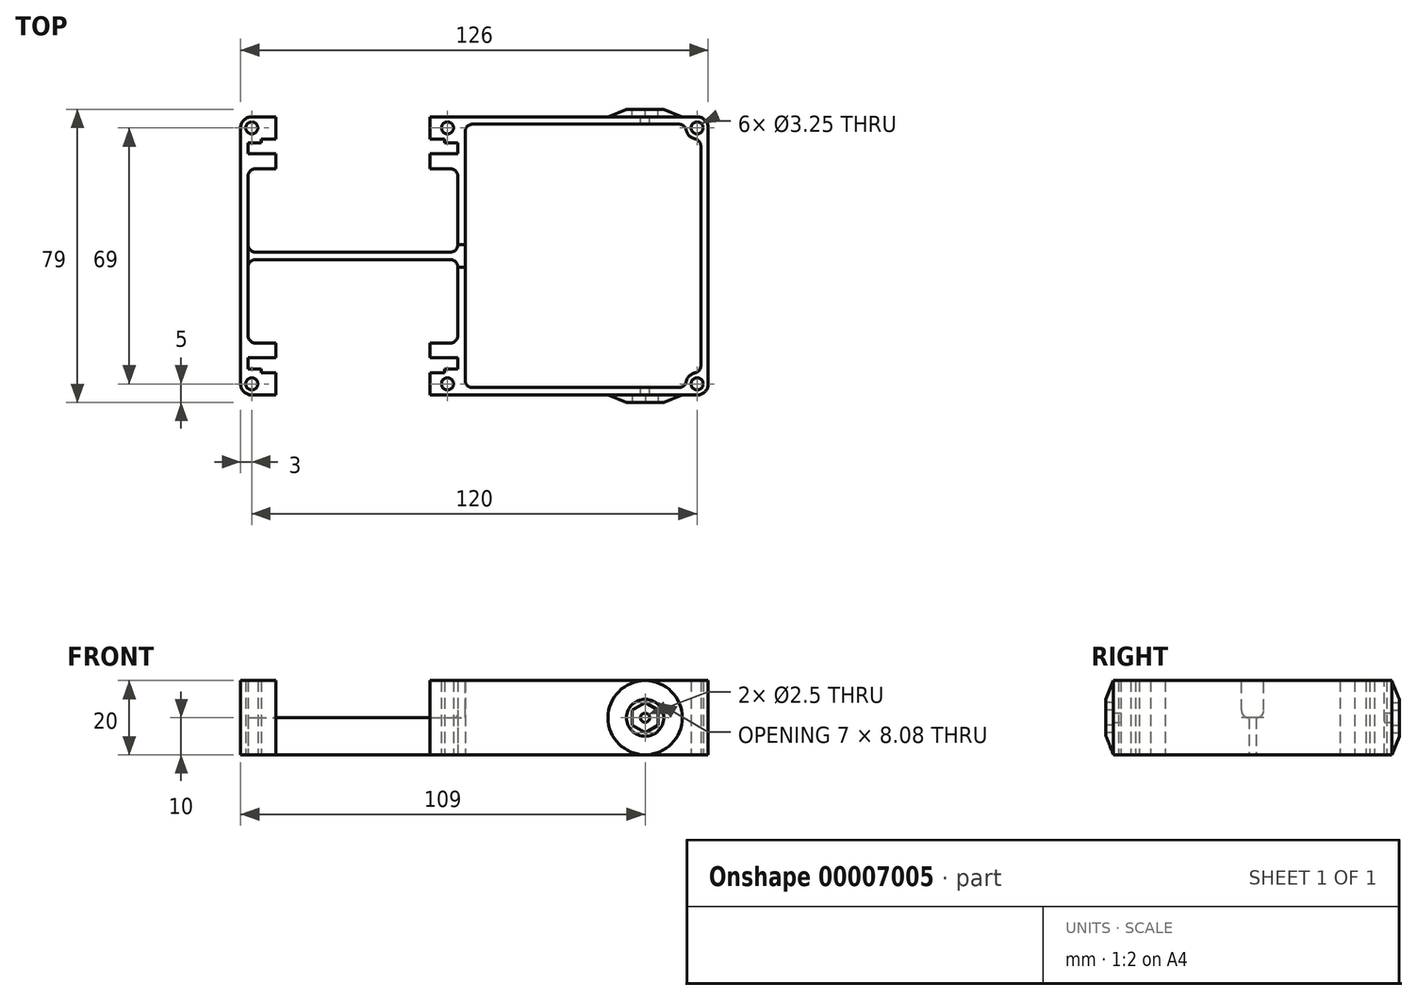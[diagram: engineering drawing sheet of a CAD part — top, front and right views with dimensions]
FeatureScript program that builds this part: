
annotation { "Feature Type Name" : "Feature", "Feature Type Description" : "" }
export const myFeature = defineFeature(function(context is Context, id is Id, definition is map)
    precondition{}
    {
        {
            var Q0;
            Q0=qCreatedBy(makeId("Top.planeOp"),FACE);
            var sketch = newSketch(context, id + "F0", { "sketchPlane" : qUnion([Q0])});
            skLineSegment(sketch, "E0.0", {"start": v(41, 72) * mm, "end": v(41, 66) * mm});
            skLineSegment(sketch, "E1.0", {"start": v(-7.5, 62) * mm, "end": v(-0.5, 62) * mm});
            skLineSegment(sketch, "E2.0", {"start": v(-8, 65) * mm, "end": v(-8, 62.5) * mm});
            skLineSegment(sketch, "E3.0", {"start": v(41, 62) * mm, "end": v(48, 62) * mm});
            skLineSegment(sketch, "E4.0", {"start": v(48.5, 62.5) * mm, "end": v(48.5, 65) * mm});
            skLineSegment(sketch, "E5.trimOffspring", {"start": v(-0.5, 66) * mm, "end": v(-0.5, 72) * mm});
            skLineSegment(sketch, "E6", {"start": v(-8, 62.5) * mm, "end": v(-8, 62) * mm});
            skLineSegment(sketch, "E7", {"start": v(-8, 62) * mm, "end": v(-7.5, 62) * mm});
            skLineSegment(sketch, "E8", {"start": v(48, 62) * mm, "end": v(48.5, 62) * mm});
            skLineSegment(sketch, "E9", {"start": v(48.5, 62) * mm, "end": v(48.5, 62.5) * mm});
            skLineSegment(sketch, "E10", {"start": v(45, 65) * mm, "end": v(48.5, 65) * mm});
            skLineSegment(sketch, "E11", {"start": v(-8, 65) * mm, "end": v(-4.5, 65) * mm});
            skLineSegment(sketch, "E12", {"start": v(-0.5, 66) * mm, "end": v(-4.5, 66) * mm});
            skLineSegment(sketch, "E13", {"start": v(-4.5, 66) * mm, "end": v(-4.5, 65) * mm});
            skLineSegment(sketch, "E14", {"start": v(41, 66) * mm, "end": v(45, 66) * mm});
            skLineSegment(sketch, "E15", {"start": v(45, 66) * mm, "end": v(45, 65) * mm});
            skLineSegment(sketch, "E16", {"start": v(-0.5, 62) * mm, "end": v(-0.5, 58) * mm});
            skLineSegment(sketch, "E17", {"start": v(41, 62) * mm, "end": v(41, 58) * mm});
            skLineSegment(sketch, "E18", {"start": v(-0.5, 58) * mm, "end": v(-8, 58) * mm});
            skLineSegment(sketch, "E19", {"start": v(41, 58) * mm, "end": v(48.5, 58) * mm});
            skLineSegment(sketch, "E20", {"start": v(-0.5, 72) * mm, "end": v(-10, 72) * mm});
            skLineSegment(sketch, "E21", {"start": v(41, 72) * mm, "end": v(116, 72) * mm});
            skLineSegment(sketch, "E22.1", {"start": v(50.5, 70) * mm, "end": v(110.17, 70) * mm});
            skPoint(sketch, "E23.endSnap0", {"position": v(41, 69) * mm});
            skCircle(sketch, "E24", {"center": v(45.75, 69) * mm, "radius": 1.63 * mm});
            skCircle(sketch, "E25", {"center": v(-7, 69) * mm, "radius": 1.63 * mm});
            skCircle(sketch, "E26", {"center": v(113, 69) * mm, "radius": 1.63 * mm});
            skArc(sketch, "E27.trimOffspring", {"start": v(110.17, 70) * mm, "mid": v(110.88, 66.88) * mm, "end": v(114, 66.17) * mm});
            skLineSegment(sketch, "E28", {"start": v(-8, 58) * mm, "end": v(-8, 35.5) * mm});
            skLineSegment(sketch, "E29", {"start": v(-8, 35.5) * mm, "end": v(48.5, 35.5) * mm});
            skLineSegment(sketch, "E30", {"start": v(48.5, 35.5) * mm, "end": v(48.5, 58) * mm});
            skLineSegment(sketch, "E31.MirrorCS", {"start": v(-8, 7) * mm, "end": v(-7.5, 7) * mm});
            skLineSegment(sketch, "E32.MirrorCS", {"start": v(48.5, 6.5) * mm, "end": v(48.5, 4) * mm});
            skLineSegment(sketch, "E33.MirrorCS", {"start": v(-8, 4) * mm, "end": v(-8, 6.5) * mm});
            skLineSegment(sketch, "E34.MirrorCS", {"start": v(-4.5, 3) * mm, "end": v(-4.5, 4) * mm});
            skLineSegment(sketch, "E35.MirrorCS", {"start": v(-0.5, 7) * mm, "end": v(-0.5, 11) * mm});
            skLineSegment(sketch, "E36.MirrorCS", {"start": v(-0.5, 3) * mm, "end": v(-4.5, 3) * mm});
            skCircle(sketch, "E37.MirrorC", {"center": v(113, 0) * mm, "radius": 1.63 * mm});
            skCircle(sketch, "E38.MirrorC", {"center": v(-7, 0) * mm, "radius": 1.63 * mm});
            skLineSegment(sketch, "E39.MirrorCS", {"start": v(45, 4) * mm, "end": v(48.5, 4) * mm});
            skLineSegment(sketch, "E40.MirrorCS", {"start": v(45, 3) * mm, "end": v(45, 4) * mm});
            skLineSegment(sketch, "E41.MirrorCS", {"start": v(-8, 4) * mm, "end": v(-4.5, 4) * mm});
            skLineSegment(sketch, "E42.MirrorCS", {"start": v(41, 7) * mm, "end": v(41, 11) * mm});
            skLineSegment(sketch, "E43.MirrorCS", {"start": v(41, 3) * mm, "end": v(45, 3) * mm});
            skLineSegment(sketch, "E44.MirrorCS", {"start": v(-0.5, -3) * mm, "end": v(-10, -3) * mm});
            skArc(sketch, "E45.MirrorCS", {"start": v(110.17, -1) * mm, "mid": v(110.88, 2.12) * mm, "end": v(114, 2.83) * mm});
            skCircle(sketch, "E46.MirrorC", {"center": v(45.75, 0) * mm, "radius": 1.63 * mm});
            skLineSegment(sketch, "E47.MirrorCS", {"start": v(-7.5, 7) * mm, "end": v(-0.5, 7) * mm});
            skLineSegment(sketch, "E48.MirrorCS", {"start": v(41, -3) * mm, "end": v(41, 3) * mm});
            skLineSegment(sketch, "E49.MirrorCS", {"start": v(-8, 33.5) * mm, "end": v(48.5, 33.5) * mm});
            skLineSegment(sketch, "E50.MirrorCS", {"start": v(41, 7) * mm, "end": v(48, 7) * mm});
            skLineSegment(sketch, "E51.MirrorCS", {"start": v(48.5, 33.5) * mm, "end": v(48.5, 11) * mm});
            skLineSegment(sketch, "E52.MirrorCS", {"start": v(-0.5, 3) * mm, "end": v(-0.5, -3) * mm});
            skPoint(sketch, "E53.MirrorP", {"position": v(41, 0) * mm});
            skLineSegment(sketch, "E54.MirrorCS", {"start": v(-0.5, 11) * mm, "end": v(-8, 11) * mm});
            skLineSegment(sketch, "E55.MirrorCS", {"start": v(41, 11) * mm, "end": v(48.5, 11) * mm});
            skLineSegment(sketch, "E56.MirrorCS", {"start": v(41, -3) * mm, "end": v(116, -3) * mm});
            skLineSegment(sketch, "E57.MirrorCS", {"start": v(-8, 11) * mm, "end": v(-8, 33.5) * mm});
            skLineSegment(sketch, "E58.MirrorCS", {"start": v(50.5, -1) * mm, "end": v(110.17, -1) * mm});
            skLineSegment(sketch, "E59", {"start": v(116, 72) * mm, "end": v(116, -3) * mm});
            skLineSegment(sketch, "E60", {"start": v(114, 2.83) * mm, "end": v(114, 66.17) * mm});
            skLineSegment(sketch, "E61", {"start": v(-10, 72) * mm, "end": v(-10, -3) * mm});
            skLineSegment(sketch, "E62", {"start": v(-8, 7) * mm, "end": v(-8, 6.5) * mm});
            skLineSegment(sketch, "E63", {"start": v(48, 7) * mm, "end": v(48.5, 7) * mm});
            skLineSegment(sketch, "E64", {"start": v(48.5, 7) * mm, "end": v(48.5, 6.5) * mm});
            skLineSegment(sketch, "E65", {"start": v(50.5, 70) * mm, "end": v(50.5, -1) * mm});
            skSolve(sketch);
        }
        {
            var Q0;
            Q0=makeQuery(id+"F0.imprint","IMPRINT",FACE,{"disambiguationData":[TD([[makeQuery(id+"F0.imprint","IMPRINT",EDGE,{"derivedFrom":sQuery(id+"F0.wireOp",EDGE,"E0.0")}),1.0]])]});
            extrude(context, id + "F1", {"entities" : qUnion([Q0]), "depth" : 20 * mm});
        }
        {
            var Q0;
            Q0=makeQuery(id+"F1.opExtrude","SWEPT_FACE",FACE,{"disambiguationData":[OSD([sQuery(id+"F0.wireOp",EDGE,"E21")])]});
            var sketch = newSketch(context, id + "F2", { "sketchPlane" : qUnion([Q0])});
            skCircle(sketch, "E66", {"center": v(-99, 10) * mm, "radius": 10 * mm});
            skPoint(sketch, "E66.centerSnap0", {"position": v(-113, 10) * mm});
            skSolve(sketch);
        }
        {
            var Q0;
            Q0=qSketchRegion(id+"F2",true);
            extrude(context, id + "F3", {"entities" : qUnion([Q0]), "operationType" : NewBodyOperationType.ADD, "depth" : 2 * mm});
        }
        {
            var Q0;
            Q0=makeQuery(id+"F3.opExtrude","CAP_EDGE",EDGE,{"disambiguationData":[OSD([sQuery(id+"F2.wireOp",EDGE,"E66")])],"isStart":false});
            chamfer(context, id + "F4", {"entities" : qUnion([Q0]), "chamferType" : ChamferType.TWO_OFFSETS, "width1" : 5 * mm, "oppositeDirection" : false, "width2" : 2 * mm, "tangentPropagation" : true});
        }
        {
            var Q0;
            Q0=makeQuery(id+"F3.opExtrude","CAP_FACE",FACE,{"disambiguationData":[OSD([sQuery(id+"F2.wireOp",EDGE,"E66")])],"isStart":false});
            var sketch = newSketch(context, id + "F5", { "sketchPlane" : qUnion([Q0])});
            skCircle(sketch, "E67", {"center": v(-99, 10) * mm, "radius": 1.25 * mm});
            skSolve(sketch);
        }
        {
            var Q0;
            Q0=makeQuery(id+"F1.opExtrude","SWEPT_FACE",FACE,{"disambiguationData":[OSD([sQuery(id+"F0.wireOp",EDGE,"E56.MirrorCS")])]});
            var sketch = newSketch(context, id + "F6", { "sketchPlane" : qUnion([Q0])});
            skCircle(sketch, "E68", {"center": v(99, 10) * mm, "radius": 10 * mm});
            skSolve(sketch);
        }
        {
            var Q0;
            Q0=qSketchRegion(id+"F6",true);
            extrude(context, id + "F7", {"entities" : qUnion([Q0]), "operationType" : NewBodyOperationType.ADD, "depth" : 2 * mm});
        }
        {
            var Q0;
            Q0=makeQuery(id+"F5.imprint","IMPRINT",FACE,{"disambiguationData":[TD([[makeQuery(id+"F5.imprint","IMPRINT",EDGE,{"derivedFrom":sQuery(id+"F5.wireOp",EDGE,"E67")}),1.0]])]});
            extrude(context, id + "F8", {"entities" : qUnion([Q0]), "operationType" : NewBodyOperationType.REMOVE, "oppositeDirection" : true, "depth" : 100 * mm});
        }
        {
            var Q0;
            Q0=makeQuery(id+"F7.opExtrude","CAP_EDGE",EDGE,{"disambiguationData":[OSD([sQuery(id+"F6.wireOp",EDGE,"E68")])],"isStart":false});
            chamfer(context, id + "F9", {"entities" : qUnion([Q0]), "chamferType" : ChamferType.TWO_OFFSETS, "width1" : 5 * mm, "oppositeDirection" : false, "width2" : 2 * mm, "tangentPropagation" : true});
        }
        {
            var Q0;
            Q0=makeQuery(id+"F1.opExtrude","SWEPT_EDGE",EDGE,{"disambiguationData":[OSD([sQuery(id+"F0.wireOp",EDGE,"E44.MirrorCS"),sQuery(id+"F0.wireOp",EDGE,"E61")])]});
            var Q1;
            Q1=makeQuery(id+"F1.opExtrude","SWEPT_EDGE",EDGE,{"disambiguationData":[OSD([sQuery(id+"F0.wireOp",EDGE,"E56.MirrorCS"),sQuery(id+"F0.wireOp",EDGE,"E59")])]});
            var Q2;
            Q2=makeQuery(id+"F1.opExtrude","SWEPT_EDGE",EDGE,{"disambiguationData":[OSD([sQuery(id+"F0.wireOp",EDGE,"E21"),sQuery(id+"F0.wireOp",EDGE,"E59")])]});
            var Q3;
            Q3=makeQuery(id+"F1.opExtrude","SWEPT_EDGE",EDGE,{"disambiguationData":[OSD([sQuery(id+"F0.wireOp",EDGE,"E20"),sQuery(id+"F0.wireOp",EDGE,"E61")])]});
            fillet(context, id + "F10", {"entities" : qUnion([Q0, Q1, Q2, Q3]), "radius" : 3 * mm, "tangentPropagation" : true, "allowEdgeOverflow" : false});
        }
        {
            var Q0;
            Q0=makeQuery(id+"F1.opExtrude","SWEPT_EDGE",EDGE,{"disambiguationData":[OSD([sQuery(id+"F0.wireOp",EDGE,"E45.MirrorCS"),sQuery(id+"F0.wireOp",EDGE,"E58.MirrorCS")])]});
            var Q1;
            Q1=makeQuery(id+"F1.opExtrude","SWEPT_EDGE",EDGE,{"disambiguationData":[OSD([sQuery(id+"F0.wireOp",EDGE,"E45.MirrorCS"),sQuery(id+"F0.wireOp",EDGE,"E60")])]});
            var Q2;
            Q2=makeQuery(id+"F1.opExtrude","SWEPT_EDGE",EDGE,{"disambiguationData":[OSD([sQuery(id+"F0.wireOp",EDGE,"E58.MirrorCS"),sQuery(id+"F0.wireOp",EDGE,"E65")])]});
            var Q3;
            Q3=makeQuery(id+"F1.opExtrude","SWEPT_EDGE",EDGE,{"disambiguationData":[OSD([sQuery(id+"F0.wireOp",EDGE,"E22.1"),sQuery(id+"F0.wireOp",EDGE,"E65")])]});
            var Q4;
            Q4=makeQuery(id+"F1.opExtrude","SWEPT_EDGE",EDGE,{"disambiguationData":[OSD([sQuery(id+"F0.wireOp",EDGE,"E22.1"),sQuery(id+"F0.wireOp",EDGE,"E27.trimOffspring")])]});
            var Q5;
            Q5=makeQuery(id+"F1.opExtrude","SWEPT_EDGE",EDGE,{"disambiguationData":[OSD([sQuery(id+"F0.wireOp",EDGE,"E27.trimOffspring"),sQuery(id+"F0.wireOp",EDGE,"E60")])]});
            var Q6;
            Q6=makeQuery(id+"F1.opExtrude","SWEPT_EDGE",EDGE,{"disambiguationData":[OSD([sQuery(id+"F0.wireOp",EDGE,"E49.MirrorCS"),sQuery(id+"F0.wireOp",EDGE,"E57.MirrorCS")])]});
            var Q7;
            Q7=makeQuery(id+"F1.opExtrude","SWEPT_EDGE",EDGE,{"disambiguationData":[OSD([sQuery(id+"F0.wireOp",EDGE,"E28"),sQuery(id+"F0.wireOp",EDGE,"E29")])]});
            var Q8;
            Q8=makeQuery(id+"F1.opExtrude","SWEPT_EDGE",EDGE,{"disambiguationData":[OSD([sQuery(id+"F0.wireOp",EDGE,"E29"),sQuery(id+"F0.wireOp",EDGE,"E30")])]});
            var Q9;
            Q9=makeQuery(id+"F1.opExtrude","SWEPT_EDGE",EDGE,{"disambiguationData":[OSD([sQuery(id+"F0.wireOp",EDGE,"E49.MirrorCS"),sQuery(id+"F0.wireOp",EDGE,"E51.MirrorCS")])]});
            var Q10;
            Q10=makeQuery(id+"F1.opExtrude","SWEPT_EDGE",EDGE,{"disambiguationData":[OSD([sQuery(id+"F0.wireOp",EDGE,"E19"),sQuery(id+"F0.wireOp",EDGE,"E30")])]});
            var Q11;
            Q11=makeQuery(id+"F1.opExtrude","SWEPT_EDGE",EDGE,{"disambiguationData":[OSD([sQuery(id+"F0.wireOp",EDGE,"E18"),sQuery(id+"F0.wireOp",EDGE,"E28")])]});
            var Q12;
            Q12=makeQuery(id+"F1.opExtrude","SWEPT_EDGE",EDGE,{"disambiguationData":[OSD([sQuery(id+"F0.wireOp",EDGE,"E54.MirrorCS"),sQuery(id+"F0.wireOp",EDGE,"E57.MirrorCS")])]});
            var Q13;
            Q13=makeQuery(id+"F1.opExtrude","SWEPT_EDGE",EDGE,{"disambiguationData":[OSD([sQuery(id+"F0.wireOp",EDGE,"E51.MirrorCS"),sQuery(id+"F0.wireOp",EDGE,"E55.MirrorCS")])]});
            fillet(context, id + "F11", {"entities" : qUnion([Q0, Q1, Q2, Q3, Q4, Q5, Q6, Q7, Q8, Q9, Q10, Q11, Q12, Q13]), "radius" : 2 * mm, "tangentPropagation" : true, "allowEdgeOverflow" : false});
        }
        {
            var Q0;
            Q0=makeQuery(id+"F3.opExtrude","CAP_FACE",FACE,{"disambiguationData":[OSD([sQuery(id+"F2.wireOp",EDGE,"E66")])],"isStart":false});
            var sketch = newSketch(context, id + "F12", { "sketchPlane" : qUnion([Q0])});
            skCircle(sketch, "E69.cCircle", {"center": v(-99, 10) * mm, "radius": 3.5 * mm, "construction": true});
            skLineSegment(sketch, "E69.0", {"start": v(-95.5, 12.02) * mm, "end": v(-95.5, 7.98) * mm});
            skLineSegment(sketch, "E69.1", {"start": v(-95.5, 7.98) * mm, "end": v(-99, 5.96) * mm});
            skLineSegment(sketch, "E69.2", {"start": v(-99, 5.96) * mm, "end": v(-102.5, 7.98) * mm});
            skLineSegment(sketch, "E69.3", {"start": v(-102.5, 7.98) * mm, "end": v(-102.5, 12.02) * mm});
            skLineSegment(sketch, "E69.4", {"start": v(-102.5, 12.02) * mm, "end": v(-99, 14.04) * mm});
            skLineSegment(sketch, "E69.5", {"start": v(-99, 14.04) * mm, "end": v(-95.5, 12.02) * mm});
            skPoint(sketch, "E69.0.midPoint", {"position": v(-95.5, 10) * mm});
            skSolve(sketch);
        }
        {
            var Q0;
            Q0=makeQuery(id+"F12.imprint","IMPRINT",FACE,{"disambiguationData":[TD([[makeQuery(id+"F12.imprint","IMPRINT",EDGE,{"derivedFrom":sQuery(id+"F12.wireOp",EDGE,"E69.0")}),-1.0]])]});
            extrude(context, id + "F13", {"entities" : qUnion([Q0]), "operationType" : NewBodyOperationType.REMOVE, "oppositeDirection" : true, "depth" : 2 * mm});
        }
        {
            var Q0;
            Q0=makeQuery(id+"F7.opExtrude","CAP_FACE",FACE,{"disambiguationData":[OSD([sQuery(id+"F6.wireOp",EDGE,"E68")])],"isStart":false});
            var sketch = newSketch(context, id + "F14", { "sketchPlane" : qUnion([Q0])});
            skCircle(sketch, "E70.cCircle", {"center": v(99, 10) * mm, "radius": 3.5 * mm, "construction": true});
            skLineSegment(sketch, "E70.0", {"start": v(95.5, 7.98) * mm, "end": v(95.5, 12.02) * mm});
            skLineSegment(sketch, "E70.1", {"start": v(95.5, 12.02) * mm, "end": v(99, 14.04) * mm});
            skLineSegment(sketch, "E70.2", {"start": v(99, 14.04) * mm, "end": v(102.5, 12.02) * mm});
            skLineSegment(sketch, "E70.3", {"start": v(102.5, 12.02) * mm, "end": v(102.5, 7.98) * mm});
            skLineSegment(sketch, "E70.4", {"start": v(102.5, 7.98) * mm, "end": v(99, 5.96) * mm});
            skLineSegment(sketch, "E70.5", {"start": v(99, 5.96) * mm, "end": v(95.5, 7.98) * mm});
            skPoint(sketch, "E70.0.midPoint", {"position": v(95.5, 10) * mm});
            skSolve(sketch);
        }
        {
            var Q0;
            Q0=qSketchRegion(id+"F14",true);
            extrude(context, id + "F15", {"entities" : qUnion([Q0]), "operationType" : NewBodyOperationType.REMOVE, "oppositeDirection" : true, "depth" : 2 * mm});
        }
        {
            var Q0;
            Q0=makeQuery(id+"F1.opExtrude","CAP_FACE",FACE,{"disambiguationData":[OSD([sQuery(id+"F0.wireOp",EDGE,"E0.0"),sQuery(id+"F0.wireOp",EDGE,"E1.0"),sQuery(id+"F0.wireOp",EDGE,"E2.0"),sQuery(id+"F0.wireOp",EDGE,"E3.0"),sQuery(id+"F0.wireOp",EDGE,"E4.0"),sQuery(id+"F0.wireOp",EDGE,"E5.trimOffspring"),sQuery(id+"F0.wireOp",EDGE,"E6"),sQuery(id+"F0.wireOp",EDGE,"E7"),sQuery(id+"F0.wireOp",EDGE,"E8"),sQuery(id+"F0.wireOp",EDGE,"E9"),sQuery(id+"F0.wireOp",EDGE,"E10"),sQuery(id+"F0.wireOp",EDGE,"E11"),sQuery(id+"F0.wireOp",EDGE,"E12"),sQuery(id+"F0.wireOp",EDGE,"E13"),sQuery(id+"F0.wireOp",EDGE,"E14"),sQuery(id+"F0.wireOp",EDGE,"E15"),sQuery(id+"F0.wireOp",EDGE,"E16"),sQuery(id+"F0.wireOp",EDGE,"E17"),sQuery(id+"F0.wireOp",EDGE,"E18"),sQuery(id+"F0.wireOp",EDGE,"E19"),sQuery(id+"F0.wireOp",EDGE,"E20"),sQuery(id+"F0.wireOp",EDGE,"E21"),sQuery(id+"F0.wireOp",EDGE,"E22.1"),sQuery(id+"F0.wireOp",EDGE,"E24"),sQuery(id+"F0.wireOp",EDGE,"E25"),sQuery(id+"F0.wireOp",EDGE,"E26"),sQuery(id+"F0.wireOp",EDGE,"E27.trimOffspring"),sQuery(id+"F0.wireOp",EDGE,"E28"),sQuery(id+"F0.wireOp",EDGE,"E29"),sQuery(id+"F0.wireOp",EDGE,"E30"),sQuery(id+"F0.wireOp",EDGE,"E31.MirrorCS"),sQuery(id+"F0.wireOp",EDGE,"E32.MirrorCS"),sQuery(id+"F0.wireOp",EDGE,"E33.MirrorCS"),sQuery(id+"F0.wireOp",EDGE,"E34.MirrorCS"),sQuery(id+"F0.wireOp",EDGE,"E35.MirrorCS"),sQuery(id+"F0.wireOp",EDGE,"E36.MirrorCS"),sQuery(id+"F0.wireOp",EDGE,"E37.MirrorC"),sQuery(id+"F0.wireOp",EDGE,"E38.MirrorC"),sQuery(id+"F0.wireOp",EDGE,"E39.MirrorCS"),sQuery(id+"F0.wireOp",EDGE,"E40.MirrorCS"),sQuery(id+"F0.wireOp",EDGE,"E41.MirrorCS"),sQuery(id+"F0.wireOp",EDGE,"E42.MirrorCS"),sQuery(id+"F0.wireOp",EDGE,"E43.MirrorCS"),sQuery(id+"F0.wireOp",EDGE,"E44.MirrorCS"),sQuery(id+"F0.wireOp",EDGE,"E45.MirrorCS"),sQuery(id+"F0.wireOp",EDGE,"E46.MirrorC"),sQuery(id+"F0.wireOp",EDGE,"E47.MirrorCS"),sQuery(id+"F0.wireOp",EDGE,"E48.MirrorCS"),sQuery(id+"F0.wireOp",EDGE,"E49.MirrorCS"),sQuery(id+"F0.wireOp",EDGE,"E50.MirrorCS"),sQuery(id+"F0.wireOp",EDGE,"E51.MirrorCS"),sQuery(id+"F0.wireOp",EDGE,"E52.MirrorCS"),sQuery(id+"F0.wireOp",EDGE,"E54.MirrorCS"),sQuery(id+"F0.wireOp",EDGE,"E55.MirrorCS"),sQuery(id+"F0.wireOp",EDGE,"E56.MirrorCS"),sQuery(id+"F0.wireOp",EDGE,"E57.MirrorCS"),sQuery(id+"F0.wireOp",EDGE,"E58.MirrorCS"),sQuery(id+"F0.wireOp",EDGE,"E59"),sQuery(id+"F0.wireOp",EDGE,"E60"),sQuery(id+"F0.wireOp",EDGE,"E61"),sQuery(id+"F0.wireOp",EDGE,"E62"),sQuery(id+"F0.wireOp",EDGE,"E63"),sQuery(id+"F0.wireOp",EDGE,"E64"),sQuery(id+"F0.wireOp",EDGE,"E65")])],"isStart":false});
            var sketch = newSketch(context, id + "F16", { "sketchPlane" : qUnion([Q0])});
            skLineSegment(sketch, "E71", {"start": v(-8, 37.5) * mm, "end": v(-8, 31.5) * mm});
            skLineSegment(sketch, "E72", {"start": v(-8, 31.5) * mm, "end": v(48.5, 31.5) * mm});
            skLineSegment(sketch, "E73", {"start": v(48.5, 37.5) * mm, "end": v(-8, 37.5) * mm});
            skLineSegment(sketch, "E74", {"start": v(48.5, 37.5) * mm, "end": v(50.5, 37.5) * mm});
            skLineSegment(sketch, "E75", {"start": v(50.5, 37.5) * mm, "end": v(50.5, 31.5) * mm});
            skLineSegment(sketch, "E76", {"start": v(50.5, 31.5) * mm, "end": v(48.5, 31.5) * mm});
            skSolve(sketch);
        }
        {
            var Q0;
            Q0=qSketchRegion(id+"F16",true);
            extrude(context, id + "F17", {"entities" : qUnion([Q0]), "operationType" : NewBodyOperationType.REMOVE, "oppositeDirection" : true, "depth" : 10 * mm});
        }
        {
            var Q0;
            Q0=makeQuery(id+"F17.boolean.opBoolean","COPY",EDGE,{"derivedFrom":makeQuery(id+"F17.opExtrude","CAP_EDGE",EDGE,{"disambiguationData":[OSD([sQuery(id+"F16.wireOp",EDGE,"E73"),sQuery(id+"F16.wireOp",EDGE,"E74")])],"isStart":false})});
            var Q1;
            Q1=makeQuery(id+"F17.boolean.opBoolean","COPY",EDGE,{"derivedFrom":makeQuery(id+"F17.opExtrude","CAP_EDGE",EDGE,{"disambiguationData":[OSD([sQuery(id+"F16.wireOp",EDGE,"E72"),sQuery(id+"F16.wireOp",EDGE,"E76")])],"isStart":false})});
            fillet(context, id + "F18", {"entities" : qUnion([Q0, Q1]), "radius" : 2 * mm, "tangentPropagation" : true, "allowEdgeOverflow" : false});
        }
    });
